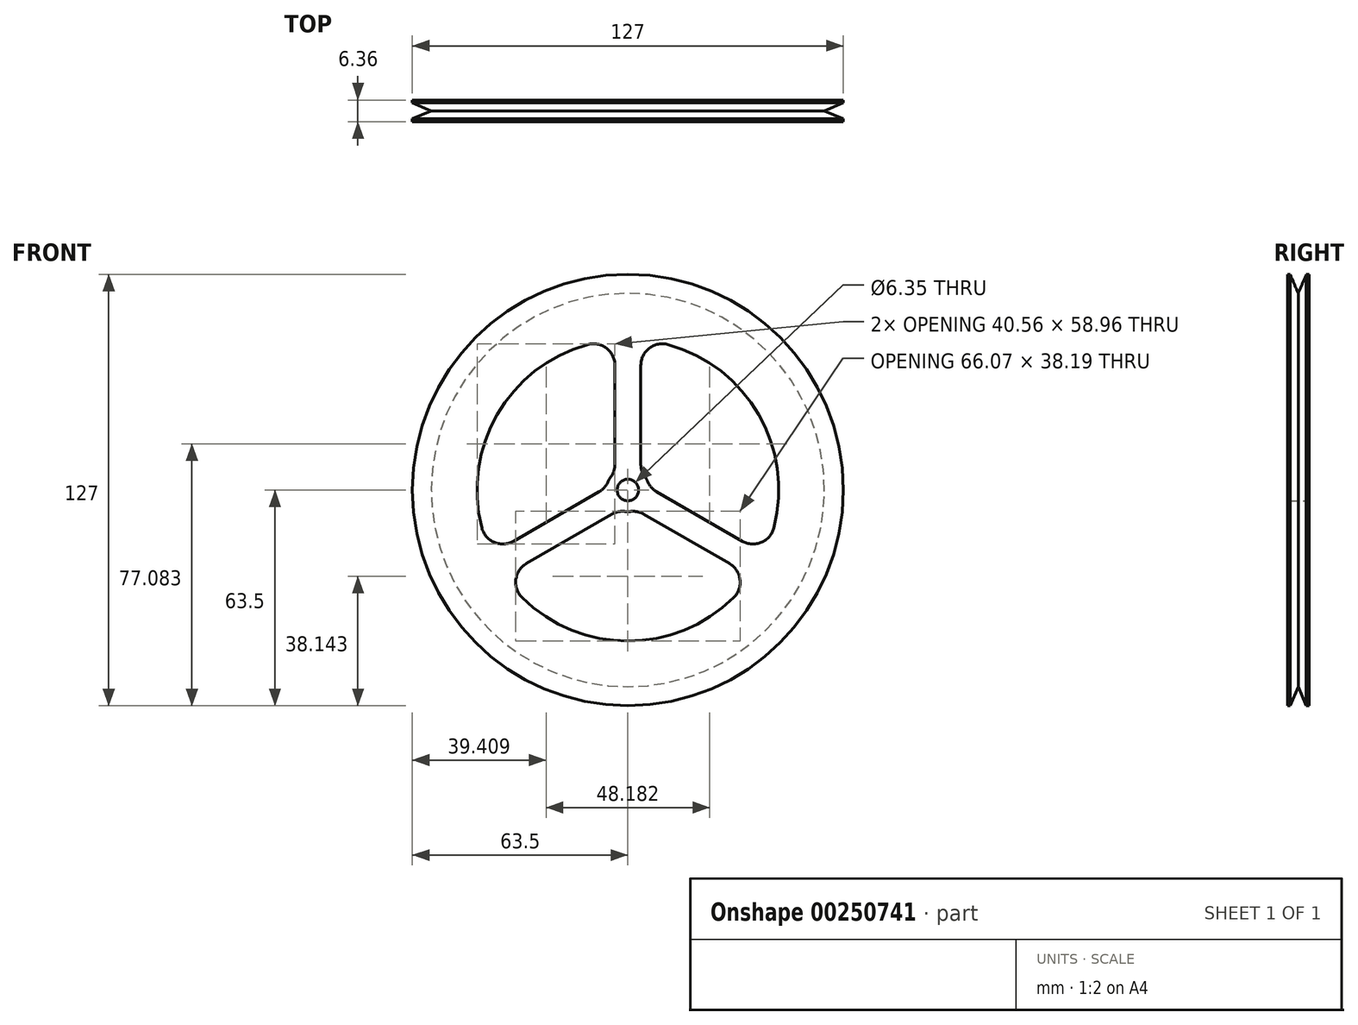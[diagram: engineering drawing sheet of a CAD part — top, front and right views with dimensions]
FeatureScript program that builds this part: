
annotation { "Feature Type Name" : "Feature", "Feature Type Description" : "" }
export const myFeature = defineFeature(function(context is Context, id is Id, definition is map)
    precondition{}
    {
        {
            var Q0;
            Q0=qCreatedBy(makeId("Front.planeOp"),FACE);
            var sketch = newSketch(context, id + "F0", { "sketchPlane" : qUnion([Q0])});
            skCircle(sketch, "E0", {"center": v(0, 0) * mm, "radius": 63.5 * mm});
            skArc(sketch, "E1.0", {"start": v(-11.85, 42.84) * mm, "mid": v(-38.5, 22.23) * mm, "end": v(-43.03, -11.15) * mm});
            skCircle(sketch, "E2", {"center": v(0, 0) * mm, "radius": 3.18 * mm});
            skArc(sketch, "E3", {"start": v(-0.76, -6.3) * mm, "mid": v(0, -6.35) * mm, "end": v(0.76, -6.3) * mm});
            skPoint(sketch, "E4.orphan", {"position": v(0, 63.5) * mm});
            skLineSegment(sketch, "E5.0", {"start": v(-3.81, 63.5) * mm, "end": v(-3.81, 63.39) * mm});
            skLineSegment(sketch, "E6.0", {"start": v(3.81, 63.5) * mm, "end": v(3.81, 63.39) * mm});
            skLineSegment(sketch, "E7.trimOffspring", {"start": v(3.81, 36.72) * mm, "end": v(3.81, 7.62) * mm});
            skLineSegment(sketch, "E8.trimOffspring", {"start": v(-3.8, 36.72) * mm, "end": v(-3.8, 7.62) * mm});
            skLineSegment(sketch, "E9.1.0", {"start": v(-29.9, -21.66) * mm, "end": v(-4.7, -7.1) * mm});
            skLineSegment(sketch, "E9.1.1", {"start": v(-33.7, -15.06) * mm, "end": v(-8.5, -0.51) * mm});
            skLineSegment(sketch, "E9.2.0", {"start": v(33.7, -15.06) * mm, "end": v(8.5, -0.51) * mm});
            skLineSegment(sketch, "E9.2.1", {"start": v(29.9, -21.66) * mm, "end": v(4.7, -7.1) * mm});
            skArc(sketch, "E10.trimOffspring", {"start": v(43.03, -11.15) * mm, "mid": v(38.5, 22.22) * mm, "end": v(11.85, 42.84) * mm});
            skArc(sketch, "E11.trimOffspring", {"start": v(-31.17, -31.69) * mm, "mid": v(0, -44.45) * mm, "end": v(31.17, -31.69) * mm});
            skArc(sketch, "E12.trimOffspring", {"start": v(-5.08, 3.81) * mm, "mid": v(-5.5, 3.18) * mm, "end": v(-5.84, 2.5) * mm});
            skArc(sketch, "E13.trimOffspring", {"start": v(5.84, 2.5) * mm, "mid": v(5.5, 3.17) * mm, "end": v(5.08, 3.8) * mm});
            skPoint(sketch, "E14.visualSharp", {"position": v(-3.81, 44.29) * mm});
            skArc(sketch, "E14.filletArc", {"start": v(-3.8, 36.72) * mm, "mid": v(-6.31, 41.77) * mm, "end": v(-11.85, 42.84) * mm});
            skPoint(sketch, "E15.visualSharp", {"position": v(-3.8, 5.08) * mm});
            skArc(sketch, "E15.filletArc", {"start": v(-5.08, 3.81) * mm, "mid": v(-4.14, 5.61) * mm, "end": v(-3.8, 7.62) * mm});
            skPoint(sketch, "E16.visualSharp", {"position": v(-6.3, 0.76) * mm});
            skArc(sketch, "E16.filletArc", {"start": v(-8.5, -0.51) * mm, "mid": v(-6.93, 0.78) * mm, "end": v(-5.84, 2.5) * mm});
            skPoint(sketch, "E17.visualSharp", {"position": v(-40.26, -18.84) * mm});
            skArc(sketch, "E17.filletArc", {"start": v(-43.03, -11.15) * mm, "mid": v(-39.33, -15.42) * mm, "end": v(-33.7, -15.06) * mm});
            skPoint(sketch, "E18.visualSharp", {"position": v(3.8, 44.29) * mm});
            skArc(sketch, "E18.filletArc", {"start": v(11.85, 42.84) * mm, "mid": v(6.31, 41.77) * mm, "end": v(3.81, 36.72) * mm});
            skPoint(sketch, "E19.visualSharp", {"position": v(3.81, 5.08) * mm});
            skArc(sketch, "E19.filletArc", {"start": v(3.81, 7.62) * mm, "mid": v(4.14, 5.61) * mm, "end": v(5.08, 3.8) * mm});
            skPoint(sketch, "E20.visualSharp", {"position": v(6.3, 0.76) * mm});
            skArc(sketch, "E20.filletArc", {"start": v(5.84, 2.5) * mm, "mid": v(6.93, 0.78) * mm, "end": v(8.5, -0.51) * mm});
            skPoint(sketch, "E21.visualSharp", {"position": v(40.26, -18.84) * mm});
            skArc(sketch, "E21.filletArc", {"start": v(33.7, -15.06) * mm, "mid": v(39.33, -15.42) * mm, "end": v(43.03, -11.15) * mm});
            skPoint(sketch, "E22.visualSharp", {"position": v(-2.5, -5.84) * mm});
            skArc(sketch, "E22.filletArc", {"start": v(-0.76, -6.3) * mm, "mid": v(-2.8, -6.39) * mm, "end": v(-4.7, -7.1) * mm});
            skPoint(sketch, "E23.visualSharp", {"position": v(2.5, -5.84) * mm});
            skArc(sketch, "E23.filletArc", {"start": v(4.7, -7.1) * mm, "mid": v(2.8, -6.39) * mm, "end": v(0.76, -6.3) * mm});
            skPoint(sketch, "E24.visualSharp", {"position": v(36.45, -25.44) * mm});
            skArc(sketch, "E24.filletArc", {"start": v(31.17, -31.69) * mm, "mid": v(33.02, -26.36) * mm, "end": v(29.9, -21.66) * mm});
            skPoint(sketch, "E25.visualSharp", {"position": v(-36.45, -25.44) * mm});
            skArc(sketch, "E25.filletArc", {"start": v(-29.9, -21.66) * mm, "mid": v(-33.02, -26.36) * mm, "end": v(-31.17, -31.69) * mm});
            skSolve(sketch);
        }
        {
            var Q0;
            Q0=makeQuery(id+"F0.imprint","IMPRINT",FACE,{"disambiguationData":[TD([[makeQuery(id+"F0.imprint","IMPRINT",EDGE,{"derivedFrom":sQuery(id+"F0.wireOp",EDGE,"E1.0")}),-1.0]])]});
            extrude(context, id + "F1", {"entities" : qUnion([Q0]), "endBound" : BoundingType.SYMMETRIC, "depth" : 6.35 * mm});
        }
        {
            var Q0;
            Q0=qCreatedBy(makeId("Right.planeOp"),FACE);
            var sketch = newSketch(context, id + "F2", { "sketchPlane" : qUnion([Q0])});
            skLineSegment(sketch, "E26", {"start": v(0, 57.91) * mm, "end": v(0, 63.5) * mm});
            skLineSegment(sketch, "E27", {"start": v(-2.38, 63.5) * mm, "end": v(0, 57.91) * mm});
            skLineSegment(sketch, "E28", {"start": v(0, 63.5) * mm, "end": v(-2.38, 63.5) * mm});
            skLineSegment(sketch, "E29.MirrorCS", {"start": v(2.38, 63.5) * mm, "end": v(0, 57.91) * mm});
            skLineSegment(sketch, "E30.MirrorCS", {"start": v(0, 63.5) * mm, "end": v(2.38, 63.5) * mm});
            skLineSegment(sketch, "E31", {"start": v(-21.93, 0) * mm, "end": v(24.84, 0) * mm, "construction": true});
            skSolve(sketch);
        }
        {
            var Q0;
            Q0 = qSketchRegion(id + "F2", true);
            var Q1;
            Q1=sQuery(id+"F2.wireOp",EDGE,"E31");
            revolve(context, id + "F3", {"operationType" : NewBodyOperationType.REMOVE, "entities" : qUnion([Q0]), "axis" : qUnion([Q1]), "revolveType" : RevolveType.FULL, "oppositeDirection" : true});
        }
    });
